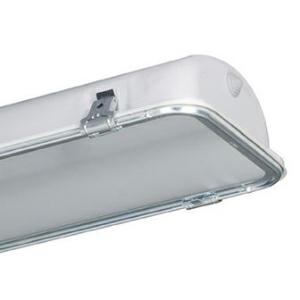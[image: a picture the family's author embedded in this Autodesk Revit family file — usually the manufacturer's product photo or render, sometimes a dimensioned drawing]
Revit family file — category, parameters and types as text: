
# Revit family: 3f_filippi_-_beta_i3f_76_vs_ampio_3f_filippi_-_55136_-_i3f_led_762x24w_ampio_vs_l1265
name_source: partatom
category: Lighting Fixtures
units: mm (PartAtom-declared; Revit-internal decimal feet)

## family parameters
Cut with Voids When Loaded = No
Host = Face
Light Source = No
Part Type = Normal
Room Calculation Point = No
Round Connector Dimension = Use Diameter
Shared = No

## types (1)
- 3F Filippi - Beta i3F 76 VS Ampio (1 x LED, 6783 lm, 54 W, 4000 K)
    Apparent Load = 54 VA
    Approval mark = ENEC
    CIE Flux Codes = 62 90 98 100 100
    Color Rendering = 80
    Color Temperature = 4000 K
    Control Gear = Electronic ballast
    Default Elevation = 1800 mm
    Description = ILLUMINOTECHNICAL
Luminous efficiency 100% (DLOR 100%, ULOR 0%).
Initial luminous flux of the luminaire 6783 lm.
Wide symmetric distribution.
Installation Interdistance Transv.D = 1.31 x hu - Long.D = 1.31 x hu.
Tabular UGR (CIE 117 - 4H-8H; S=0.25H; 70/50/20): RUG 19.7 - 20.9.
Beam angle: 90° - 99°.
Luminous efficacy 126 lm/W.
Lifetime (L93/B10): 30000 h. (tq+25°C)
Lifetime (L90/B10): 50000 h. (tq+25°C)
Lifetime (L85/B10): 80000 h. (tq+25°C)
Lifetime (L80/B10): 100000 h. (tq+25°C)
Lifetime (L85/B10): 50000 h. (tq+35°C)
Sudden decreased luminous flux after 50000 hours: 0% (C0).
Photobiological safety in compliance with IEC/TR 62778: RG0 risk exempt, (IEC 62471).
In compliance with IEC/EN 62722-2-1 - IEC/EN 62717 standards.

SOURCE
2 linear LED modules 24W/840.
Energy efficiency class (UE 2019/2020 - UE 2019/2015): D.
CIE 13.3 Colour rendering index: CRI >80 (R9 <50%).
IES TM-30 Fidelity Index: Rf = 84 Rg = 95.
CCT nominal colour temperature 4000 K.
Colour initial tolerance (MacAdam): SDCM 3.

MECHANICAL
Single-piece housing in pressed steel, powder-coated in white epoxy-polyester.
Moulded anti-glare glass, non-combustible, tempered, mounted and locked to the single-piece galvanised steel perimetrical frame, sealing gasket, hinged opening by means of galvanised steel clips.
Wide flow recuperator, oversized, in specular aluminium with superficial titanium-magnesium treatment, non-iridescent.
Gear-tray unit in hot-galvanised steel, painted in white polyester, fixed to the housing by means of "Ribloc" rapid devices in galvanised steel, hinged opening.
Luminaire with limited surface temperature. - D - (EN 60598-2-24)
Dimensions: 1265x235 mm, height 105 mm. Weight 8 kg.
IP65 protection degree.
Mechanical strength to impacts IK09 (10 joule).
Glow-wire test resistance 960°C.

ELECTRICAL
Halogen Free electronic wiring 230V-50/60Hz, power factor 0.97, THD <25%, constant output current, SELV, class I, 1 driver.
Power of the luminaire 54 W.
CE - IEC 60598-1 - EN 60598-1.
SAFE FLICKER: PstLM=<1 and SVM=<0.4 (IEC TR 61547-1 and IEC TR 63158), to ensure a more comfortable and safe light.
Luminaire compliant with EN 60598-2-22 for power supply from a centralised emergency system CPSS (Central Power Supply System), not incorporated in the luminaire - high risk areas excluded. The default power and flux are 100% in AC and 100% in DC.
Ambient temperature from -20°C to +35°C.
Temperature class T6 max 85°C.
Relative humidity UR: <85%.

INSTALLATION
Ceiling / Suspended / Wall.
All accessories dedicated to this product are available on the Catalog and on our website www.3F-Filippi.com.

APPLICATIONS
In industrial environments, stores and dry, dusty indoor environments, subject to occasional water splashes.

WARNING
Fixture not suitable for cold stores with an ambient temperature <0°C and/or relative humidity >85%.
Luminaire designed for disposal/recycling at end-of-life.
Replaceable (LED only) light source by a professional. Replaceable control gear by a professional.
    Height = 105 mm
    Lamp = 1 x LED
    Lamp Light Flux = 6783 lm
    Lamp Power = 54 W
    Lamp count = 1
    Length = 1265 mm
    Lifetime = 50000 h
    Luminous efficacy = 126 lm/W
    Manufacturer = 3F Filippi
    ModVariant = No
    Model = 3F Filippi - 55136 - i3F LED 762x24W AMPIO VS L1265
    Mounting Place = Ceiling
    Mounting Type = Pendant
    Number of Poles = 1
    OnlyDefault = Yes
    Power Factor = 1
    Product Name = 3F Filippi - Beta i3F 76 VS Ampio
    Product group = pendant luminaire
    ProductGroupID = 9
    Protection Class = Protection class I
    Protection Degree = IP 65
    RLX_Detail_Level = 1
    RLX_Emergency_Light_Flux = 0 lm
    RLX_Emergency_Type = 0
    RLX_Emergency_Type_DB = No
    RlxData = <blob elided: 64577 chars, md5=b14ecf93>
    Socket = socket
    Standby Power = 0 W
    System Light Flux = 6783 lm
    System Power = 54 W
    Type Comments = Product without accessories
    Type Image = 3ffilippi_55136.jpg
    URL = http://relux.com
    VarID = ---
    Voltage = 0 V
    Weight = 0.00 kg
    Width = 235 mm

## geometry (parser evidence)
native form markers: Blend x4, Sweep x11
no freeform markers — native parametric forms only
